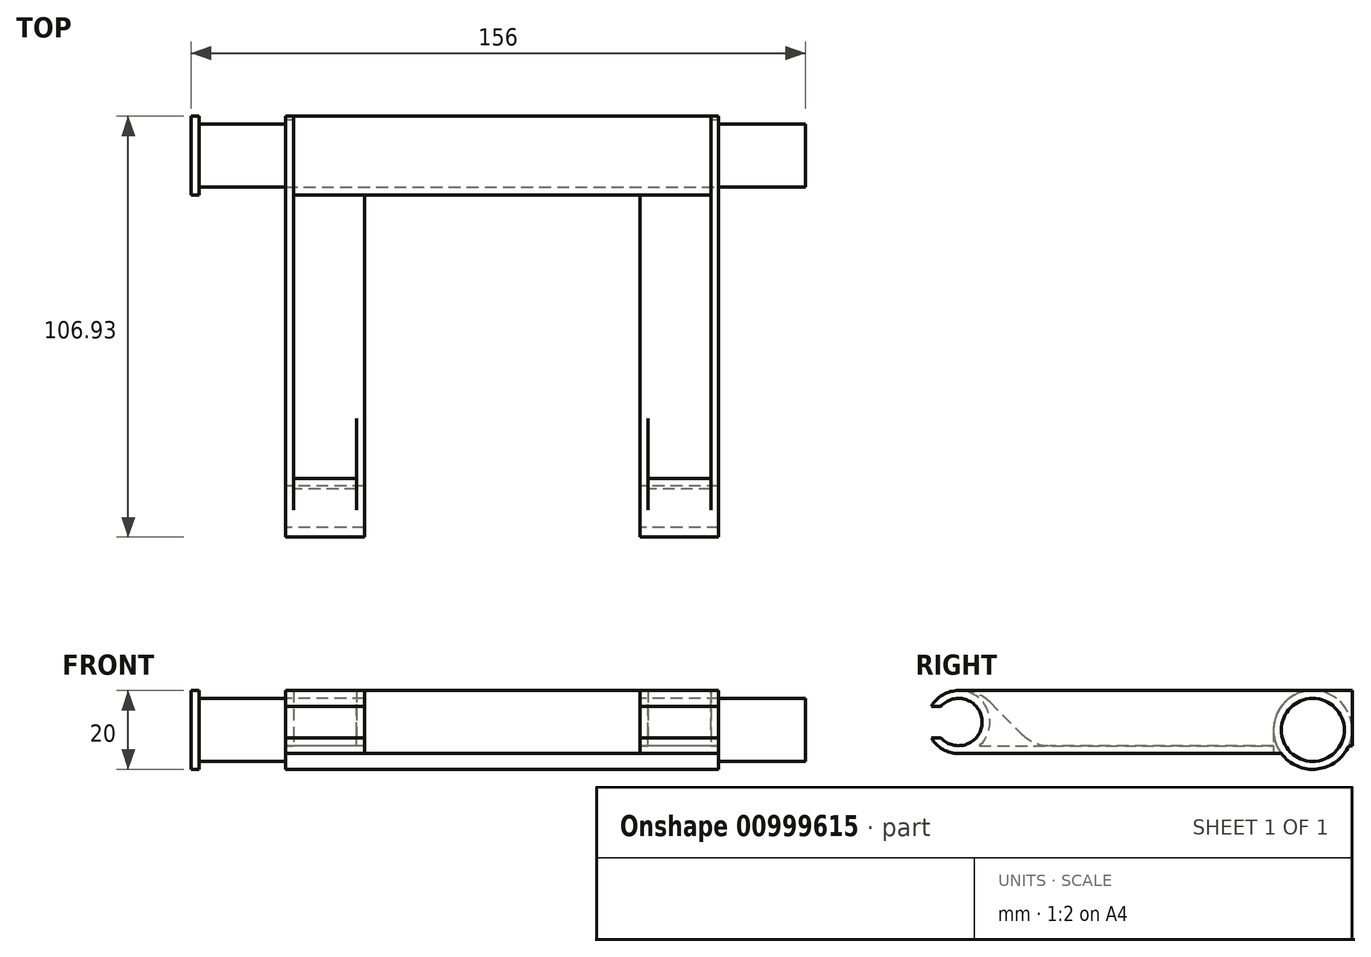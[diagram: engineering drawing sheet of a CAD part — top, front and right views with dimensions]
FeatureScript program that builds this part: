
annotation { "Feature Type Name" : "Feature", "Feature Type Description" : "" }
export const myFeature = defineFeature(function(context is Context, id is Id, definition is map)
    precondition{}
    {
        {
            var Q0;
            Q0=qCreatedBy(makeId("Top.planeOp"),FACE);
            var sketch = newSketch(context, id + "F0", { "sketchPlane" : qUnion([Q0])});
            skLineSegment(sketch, "E0.bottom", {"start": v(55, 40) * mm, "end": v(-55, 40) * mm});
            skLineSegment(sketch, "E0.top", {"start": v(55, -40) * mm, "end": v(-55, -40) * mm});
            skLineSegment(sketch, "E0.left", {"start": v(55, 40) * mm, "end": v(55, -40) * mm});
            skLineSegment(sketch, "E0.right", {"start": v(-55, 40) * mm, "end": v(-55, -40) * mm});
            skPoint(sketch, "E0.middle", {"position": v(0, 0) * mm});
            skLineSegment(sketch, "E1", {"start": v(-55, 40) * mm, "end": v(-55, 60) * mm});
            skLineSegment(sketch, "E2", {"start": v(-55, 60) * mm, "end": v(55, 60) * mm});
            skLineSegment(sketch, "E3", {"start": v(55, 60) * mm, "end": v(55, 40) * mm});
            skSolve(sketch);
        }
        {
            var Q0;
            Q0=makeQuery(id+"F0.imprint","IMPRINT",FACE,{"disambiguationData":[TD([[makeQuery(id+"F0.imprint","IMPRINT",EDGE,{"derivedFrom":sQuery(id+"F0.wireOp",EDGE,"E0.bottom")}),1.0]])]});
            extrude(context, id + "F1", {"entities" : qUnion([Q0]), "depth" : 2 * mm, "offsetDistance" : 25 * mm});
        }
        {
            var Q0;
            Q0=makeQuery(id+"F0.imprint","IMPRINT",FACE,{"disambiguationData":[TD([[makeQuery(id+"F0.imprint","IMPRINT",EDGE,{"derivedFrom":sQuery(id+"F0.wireOp",EDGE,"E0.bottom")}),-1.0]])]});
            extrude(context, id + "F2", {"entities" : qUnion([Q0]), "operationType" : NewBodyOperationType.ADD, "depth" : 16 * mm, "offsetDistance" : 25 * mm});
        }
        {
            var Q0;
            Q0=makeQuery(id+"F0.imprint","IMPRINT",FACE,{"disambiguationData":[TD([[makeQuery(id+"F0.imprint","IMPRINT",EDGE,{"derivedFrom":sQuery(id+"F0.wireOp",EDGE,"E0.bottom")}),-1.0]])]});
            extrude(context, id + "F3", {"entities" : qUnion([Q0]), "operationType" : NewBodyOperationType.ADD, "oppositeDirection" : true, "depth" : 4 * mm, "offsetDistance" : 25 * mm});
        }
        {
            var Q0;
            Q0=qCreatedBy(makeId("Right.planeOp"),FACE);
            var sketch = newSketch(context, id + "F4", { "sketchPlane" : qUnion([Q0])});
            skLineSegment(sketch, "E4.0.0", {"start": v(60, 16) * mm, "end": v(60, -4) * mm});
            skLineSegment(sketch, "E4.0.1", {"start": v(60, -4) * mm, "end": v(40, -4) * mm});
            skLineSegment(sketch, "E4.0.2", {"start": v(40, -4) * mm, "end": v(40, 0) * mm});
            skLineSegment(sketch, "E4.0.3", {"start": v(40, 0) * mm, "end": v(-40, 0) * mm});
            skLineSegment(sketch, "E4.0.4", {"start": v(-40, 0) * mm, "end": v(-40, 2) * mm});
            skLineSegment(sketch, "E4.0.5", {"start": v(-40, 2) * mm, "end": v(40, 2) * mm, "construction": true});
            skLineSegment(sketch, "E4.0.6", {"start": v(40, 2) * mm, "end": v(40, 16) * mm});
            skLineSegment(sketch, "E4.0.7", {"start": v(40, 16) * mm, "end": v(60, 16) * mm});
            skCircle(sketch, "E5", {"center": v(50, 6) * mm, "radius": 10 * mm});
            skPoint(sketch, "E5.centerSnap0", {"position": v(50, 16) * mm});
            skPoint(sketch, "E5.centerSnap1", {"position": v(60, 6) * mm});
            skCircle(sketch, "E6", {"center": v(50, 6) * mm, "radius": 8 * mm});
            skLineSegment(sketch, "E7", {"start": v(40, 0) * mm, "end": v(42, 0) * mm});
            skLineSegment(sketch, "E8", {"start": v(40, 2) * mm, "end": v(40, 0) * mm});
            skLineSegment(sketch, "E9", {"start": v(-40, 2) * mm, "end": v(-40, 8) * mm, "construction": true});
            skCircle(sketch, "E10", {"center": v(-40, 8) * mm, "radius": 8 * mm});
            skCircle(sketch, "E11", {"center": v(-40, 8) * mm, "radius": 6 * mm});
            skLineSegment(sketch, "E12", {"start": v(-40, 4) * mm, "end": v(-50.32, 4) * mm});
            skLineSegment(sketch, "E13", {"start": v(-40, 8) * mm, "end": v(-48, 8) * mm, "construction": true});
            skLineSegment(sketch, "E14.MirrorCS", {"start": v(-40, 12) * mm, "end": v(-50.32, 12) * mm});
            skSolve(sketch);
        }
        {
            var Q0;
            {var subQ0=sQuery(id+"F4.wireOp",EDGE,"E4.0.7");var subQ1=sQuery(id+"F4.wireOp",EDGE,"E4.0.0");var subQ2=makeQuery(id+"F4.imprint","INTERSECT",VERTEX,{"derivedFrom":[subQ1,subQ0]});Q0=makeQuery(id+"F4.imprint","IMPRINT",FACE,{"disambiguationData":[TD([[makeQuery(id+"F4.imprint","IMPRINT",EDGE,{"disambiguationData":[TD([[subQ2,-1.0]])],"derivedFrom":subQ1}),-1.0]])]});}
            var Q1;
            {var subQ0=sQuery(id+"F4.wireOp",EDGE,"E4.0.1");var subQ1=sQuery(id+"F4.wireOp",EDGE,"E4.0.0");var subQ2=makeQuery(id+"F4.imprint","INTERSECT",VERTEX,{"derivedFrom":[subQ1,subQ0]});Q1=makeQuery(id+"F4.imprint","IMPRINT",FACE,{"disambiguationData":[TD([[makeQuery(id+"F4.imprint","IMPRINT",EDGE,{"disambiguationData":[TD([[subQ2,1.0]])],"derivedFrom":subQ1}),-1.0]])]});}
            var Q2;
            {var subQ0=sQuery(id+"F4.wireOp",EDGE,"E4.0.2");Q2=makeQuery(id+"F4.imprint","IMPRINT",FACE,{"disambiguationData":[TD([[makeQuery(id+"F4.imprint","IMPRINT",EDGE,{"derivedFrom":subQ0}),-1.0]])]});}
            var Q3;
            {var subQ0=sQuery(id+"F4.wireOp",EDGE,"E4.0.7");var subQ1=sQuery(id+"F4.wireOp",EDGE,"E4.0.6");var subQ2=makeQuery(id+"F4.imprint","INTERSECT",VERTEX,{"derivedFrom":[subQ1,subQ0]});Q3=makeQuery(id+"F4.imprint","IMPRINT",FACE,{"disambiguationData":[TD([[makeQuery(id+"F4.imprint","IMPRINT",EDGE,{"disambiguationData":[TD([[subQ2,1.0]])],"derivedFrom":subQ1}),-1.0]])]});}
            extrude(context, id + "F5", {"entities" : qUnion([Q0, Q1, Q2, Q3]), "operationType" : NewBodyOperationType.REMOVE, "endBound" : BoundingType.SYMMETRIC, "oppositeDirection" : true, "depth" : 200 * mm, "offsetDistance" : 25 * mm});
        }
        {
            var Q0;
            Q0=makeQuery(id+"F4.imprint","IMPRINT",FACE,{"disambiguationData":[TD([[makeQuery(id+"F4.imprint","IMPRINT",EDGE,{"derivedFrom":sQuery(id+"F4.wireOp",EDGE,"E6")}),1.0]])]});
            extrude(context, id + "F6", {"entities" : qUnion([Q0]), "operationType" : NewBodyOperationType.ADD, "endBound" : BoundingType.SYMMETRIC, "depth" : 154 * mm, "offsetDistance" : 25 * mm});
        }
        {
            var Q0;
            Q0=makeQuery(id+"F6.opExtrude","CAP_FACE",FACE,{"disambiguationData":[OSD([sQuery(id+"F4.wireOp",EDGE,"E6")])],"isStart":true});
            var sketch = newSketch(context, id + "F7", { "sketchPlane" : qUnion([Q0])});
            skCircle(sketch, "E15", {"center": v(-50, 6) * mm, "radius": 10 * mm});
            skSolve(sketch);
        }
        {
            var Q0;
            Q0=makeQuery(id+"F7.imprint","IMPRINT",FACE,{"disambiguationData":[TD([[makeQuery(id+"F7.imprint","IMPRINT",EDGE,{"derivedFrom":sQuery(id+"F7.wireOp",EDGE,"E15")}),1.0]])]});
            var Q1;
            Q1=makeQuery(id+"F7.imprint","IMPRINT",FACE,{"disambiguationData":[TD([[makeQuery(id+"F7.imprint","IMPRINT",EDGE,{"derivedFrom":makeQuery(id+"F6.opExtrude","CAP_EDGE",EDGE,{"disambiguationData":[OSD([sQuery(id+"F4.wireOp",EDGE,"E6")])],"isStart":true})}),-1.0]])]});
            extrude(context, id + "F8", {"entities" : qUnion([Q0, Q1]), "operationType" : NewBodyOperationType.ADD, "depth" : 2 * mm, "offsetDistance" : 25 * mm});
        }
        {
            var Q0;
            Q0=makeQuery(id+"F1.opExtrude","CAP_FACE",FACE,{"disambiguationData":[OSD([sQuery(id+"F0.wireOp",EDGE,"E0.bottom"),sQuery(id+"F0.wireOp",EDGE,"E0.top"),sQuery(id+"F0.wireOp",EDGE,"E0.left"),sQuery(id+"F0.wireOp",EDGE,"E0.right")])],"isStart":false});
            var sketch = newSketch(context, id + "F9", { "sketchPlane" : qUnion([Q0])});
            skLineSegment(sketch, "E16", {"start": v(-55, 60) * mm, "end": v(55, 60) * mm});
            skLineSegment(sketch, "E17", {"start": v(-55, 60) * mm, "end": v(-55, -40) * mm});
            skLineSegment(sketch, "E18", {"start": v(-55, -40) * mm, "end": v(-53, -40) * mm});
            skLineSegment(sketch, "E19", {"start": v(-53, -40) * mm, "end": v(-53, 60) * mm});
            skLineSegment(sketch, "E20", {"start": v(55, 60) * mm, "end": v(55, -40) * mm});
            skLineSegment(sketch, "E21", {"start": v(55, -40) * mm, "end": v(53, -40) * mm});
            skLineSegment(sketch, "E22", {"start": v(53, -40) * mm, "end": v(53, 60) * mm});
            skLineSegment(sketch, "E23", {"start": v(-55, 50) * mm, "end": v(55, 50) * mm});
            skLineSegment(sketch, "E24", {"start": v(-35, -40) * mm, "end": v(-35, 40) * mm});
            skLineSegment(sketch, "E25", {"start": v(-35, -40) * mm, "end": v(-37, -40) * mm});
            skLineSegment(sketch, "E26", {"start": v(-37, -40) * mm, "end": v(-37, 40) * mm});
            skLineSegment(sketch, "E27", {"start": v(-37, 40) * mm, "end": v(-35, 40) * mm});
            skLineSegment(sketch, "E28", {"start": v(-37, 40) * mm, "end": v(-37, 50) * mm});
            skLineSegment(sketch, "E29", {"start": v(-35, 40) * mm, "end": v(-35, 50) * mm});
            skLineSegment(sketch, "E30", {"start": v(0, 0) * mm, "end": v(0, 23.43) * mm, "construction": true});
            skLineSegment(sketch, "E31.MirrorCS", {"start": v(37, -40) * mm, "end": v(37, 40) * mm});
            skLineSegment(sketch, "E32.MirrorCS", {"start": v(35, -40) * mm, "end": v(35, 40) * mm});
            skLineSegment(sketch, "E33.MirrorCS", {"start": v(35, -40) * mm, "end": v(37, -40) * mm});
            skLineSegment(sketch, "E34.MirrorCS", {"start": v(37, 40) * mm, "end": v(35, 40) * mm});
            skLineSegment(sketch, "E35.MirrorCS", {"start": v(37, 40) * mm, "end": v(37, 50) * mm});
            skLineSegment(sketch, "E36.MirrorCS", {"start": v(35, 40) * mm, "end": v(35, 50) * mm});
            skLineSegment(sketch, "E37", {"start": v(-37, -15) * mm, "end": v(-35, -15) * mm});
            skLineSegment(sketch, "E38.MirrorCS", {"start": v(37, -15) * mm, "end": v(35, -15) * mm});
            skSolve(sketch);
        }
        {
            var Q0;
            {var subQ0=sQuery(id+"F9.wireOp",EDGE,"E18");Q0=makeQuery(id+"F9.imprint","IMPRINT",FACE,{"disambiguationData":[TD([[makeQuery(id+"F9.imprint","IMPRINT",EDGE,{"derivedFrom":subQ0}),-1.0]])]});}
            var Q1;
            {var subQ0=sQuery(id+"F9.wireOp",EDGE,"E17");var subQ1=makeQuery(id+"F1.opExtrude","CAP_EDGE",EDGE,{"disambiguationData":[OSD([sQuery(id+"F0.wireOp",EDGE,"E0.bottom")])],"isStart":false});var subQ2=makeQuery(id+"F9.imprint","INTERSECT",VERTEX,{"derivedFrom":[subQ1,subQ0]});Q1=makeQuery(id+"F9.imprint","IMPRINT",FACE,{"disambiguationData":[TD([[makeQuery(id+"F9.imprint","IMPRINT",EDGE,{"disambiguationData":[TD([[subQ2,1.0]])],"derivedFrom":subQ0}),1.0]])]});}
            var Q2;
            {var subQ0=sQuery(id+"F9.wireOp",EDGE,"E21");Q2=makeQuery(id+"F9.imprint","IMPRINT",FACE,{"disambiguationData":[TD([[makeQuery(id+"F9.imprint","IMPRINT",EDGE,{"derivedFrom":subQ0}),-1.0]])]});}
            var Q3;
            {var subQ0=sQuery(id+"F9.wireOp",EDGE,"E20");var subQ1=makeQuery(id+"F1.opExtrude","CAP_EDGE",EDGE,{"disambiguationData":[OSD([sQuery(id+"F0.wireOp",EDGE,"E0.bottom")])],"isStart":false});var subQ2=makeQuery(id+"F9.imprint","INTERSECT",VERTEX,{"derivedFrom":[subQ1,subQ0]});Q3=makeQuery(id+"F9.imprint","IMPRINT",FACE,{"disambiguationData":[TD([[makeQuery(id+"F9.imprint","IMPRINT",EDGE,{"disambiguationData":[TD([[subQ2,1.0]])],"derivedFrom":subQ0}),-1.0]])]});}
            var Q4;
            {var subQ0=sQuery(id+"F9.wireOp",EDGE,"E25");Q4=makeQuery(id+"F9.imprint","IMPRINT",FACE,{"disambiguationData":[TD([[makeQuery(id+"F9.imprint","IMPRINT",EDGE,{"derivedFrom":subQ0}),-1.0]])]});}
            var Q5;
            {var subQ0=sQuery(id+"F9.wireOp",EDGE,"E33.MirrorCS");Q5=makeQuery(id+"F9.imprint","IMPRINT",FACE,{"disambiguationData":[TD([[makeQuery(id+"F9.imprint","IMPRINT",EDGE,{"derivedFrom":subQ0}),-1.0]])]});}
            extrude(context, id + "F10", {"entities" : qUnion([Q0, Q1, Q2, Q3, Q4, Q5]), "operationType" : NewBodyOperationType.ADD, "depth" : 14 * mm, "offsetDistance" : 25 * mm});
        }
        {
            var Q0;
            {var subQ1=sQuery(id+"F4.wireOp",EDGE,"E4.0.4");var subQ3=sQuery(id+"F4.wireOp",EDGE,"E11");var subQ4=makeQuery(id+"F4.imprint","INTERSECT",VERTEX,{"derivedFrom":[subQ1,subQ3]});Q0=makeQuery(id+"F4.imprint","IMPRINT",FACE,{"disambiguationData":[TD([[makeQuery(id+"F4.imprint","IMPRINT",EDGE,{"disambiguationData":[TD([[subQ4,1.0]])],"derivedFrom":subQ3}),-1.0]])]});}
            var Q1;
            {var subQ0=sQuery(id+"F4.wireOp",EDGE,"E4.0.4");Q1=makeQuery(id+"F4.imprint","IMPRINT",FACE,{"disambiguationData":[TD([[makeQuery(id+"F4.imprint","IMPRINT",EDGE,{"derivedFrom":subQ0}),-1.0]])]});}
            extrude(context, id + "F11", {"entities" : qUnion([Q0, Q1]), "operationType" : NewBodyOperationType.ADD, "endBound" : BoundingType.SYMMETRIC, "depth" : 110 * mm, "offsetDistance" : 25 * mm});
        }
        {
            var Q0;
            {var subQ3=sQuery(id+"F4.wireOp",EDGE,"E11");var subQ5=makeQuery(id+"F4.imprint","INTERSECT",VERTEX,{"derivedFrom":[subQ3,sQuery(id+"F4.wireOp",EDGE,"E14.MirrorCS")]});Q0=makeQuery(id+"F4.imprint","IMPRINT",FACE,{"disambiguationData":[TD([[makeQuery(id+"F4.imprint","IMPRINT",EDGE,{"disambiguationData":[TD([[subQ5,-1.0]])],"derivedFrom":subQ3}),1.0]])]});}
            var Q1;
            {var subQ1=sQuery(id+"F4.wireOp",EDGE,"E4.0.4");var subQ3=sQuery(id+"F4.wireOp",EDGE,"E11");var subQ4=makeQuery(id+"F4.imprint","INTERSECT",VERTEX,{"derivedFrom":[subQ1,subQ3]});Q1=makeQuery(id+"F4.imprint","IMPRINT",FACE,{"disambiguationData":[TD([[makeQuery(id+"F4.imprint","IMPRINT",EDGE,{"disambiguationData":[TD([[subQ4,-1.0]])],"derivedFrom":subQ3}),1.0]])]});}
            var Q2;
            {var subQ1=sQuery(id+"F4.wireOp",EDGE,"E4.0.4");var subQ3=sQuery(id+"F4.wireOp",EDGE,"E11");var subQ4=makeQuery(id+"F4.imprint","INTERSECT",VERTEX,{"derivedFrom":[subQ1,subQ3]});Q2=makeQuery(id+"F4.imprint","IMPRINT",FACE,{"disambiguationData":[TD([[makeQuery(id+"F4.imprint","IMPRINT",EDGE,{"disambiguationData":[TD([[subQ4,1.0]])],"derivedFrom":subQ3}),1.0]])]});}
            extrude(context, id + "F12", {"entities" : qUnion([Q0, Q1, Q2]), "operationType" : NewBodyOperationType.REMOVE, "endBound" : BoundingType.SYMMETRIC, "oppositeDirection" : true, "depth" : 200 * mm, "offsetDistance" : 25 * mm});
        }
        {
            var Q0;
            {var subQ0=sQuery(id+"F0.wireOp",EDGE,"E0.bottom");Q0=makeQuery(id+"F5.boolean.opBoolean","MERGE",FACE,{"derivedFrom":[makeQuery(id+"F2.boolean.opBoolean","MERGE",FACE,{"derivedFrom":[makeQuery(id+"F1.opExtrude","CAP_FACE",FACE,{"disambiguationData":[OSD([subQ0,sQuery(id+"F0.wireOp",EDGE,"E0.top"),sQuery(id+"F0.wireOp",EDGE,"E0.left"),sQuery(id+"F0.wireOp",EDGE,"E0.right")])],"isStart":true}),makeQuery(id+"F2.opExtrude","CAP_FACE",FACE,{"disambiguationData":[OSD([subQ0,sQuery(id+"F0.wireOp",EDGE,"E1"),sQuery(id+"F0.wireOp",EDGE,"E2"),sQuery(id+"F0.wireOp",EDGE,"E3")])],"isStart":true})]})],"fromTools":[makeQuery(id+"F5.opExtrude","SWEPT_FACE",FACE,{"disambiguationData":[OSD([sQuery(id+"F4.wireOp",EDGE,"E7")])]})]});}
            var sketch = newSketch(context, id + "F13", { "sketchPlane" : qUnion([Q0])});
            skLineSegment(sketch, "E39.0", {"start": v(-55, -42) * mm, "end": v(55, -42) * mm});
            skLineSegment(sketch, "E40.0", {"start": v(55, -42) * mm, "end": v(55, 40) * mm});
            skLineSegment(sketch, "E41.0", {"start": v(-55, -42) * mm, "end": v(-55, 40) * mm});
            skLineSegment(sketch, "E42.0", {"start": v(55, 40) * mm, "end": v(-55, 40) * mm});
            skLineSegment(sketch, "E43.0", {"start": v(55, 46.93) * mm, "end": v(-55, 46.93) * mm});
            skLineSegment(sketch, "E44", {"start": v(-35, 46.93) * mm, "end": v(-35, -42) * mm});
            skLineSegment(sketch, "E45", {"start": v(35, 46.93) * mm, "end": v(35, -42) * mm});
            skLineSegment(sketch, "E46", {"start": v(55, -60) * mm, "end": v(-55, -60) * mm});
            skLineSegment(sketch, "E47.0", {"start": v(-53, -40) * mm, "end": v(53, -40) * mm});
            skSolve(sketch);
        }
        {
            var Q0;
            {var subQ0=sQuery(id+"F13.wireOp",EDGE,"E45");var subQ1=sQuery(id+"F13.wireOp",EDGE,"E42.0");var subQ2=makeQuery(id+"F13.imprint","INTERSECT",VERTEX,{"derivedFrom":[subQ1,subQ0]});Q0=makeQuery(id+"F13.imprint","IMPRINT",FACE,{"disambiguationData":[TD([[makeQuery(id+"F13.imprint","IMPRINT",EDGE,{"disambiguationData":[TD([[subQ2,-1.0]])],"derivedFrom":subQ1}),1.0]])]});}
            var Q1;
            {var subQ0=sQuery(id+"F13.wireOp",EDGE,"E45");var subQ1=sQuery(id+"F13.wireOp",EDGE,"E42.0");var subQ2=makeQuery(id+"F13.imprint","INTERSECT",VERTEX,{"derivedFrom":[subQ1,subQ0]});Q1=makeQuery(id+"F13.imprint","IMPRINT",FACE,{"disambiguationData":[TD([[makeQuery(id+"F13.imprint","IMPRINT",EDGE,{"disambiguationData":[TD([[subQ2,-1.0]])],"derivedFrom":subQ1}),-1.0]])]});}
            extrude(context, id + "F14", {"entities" : qUnion([Q0, Q1]), "operationType" : NewBodyOperationType.REMOVE, "oppositeDirection" : true, "depth" : 25 * mm, "offsetDistance" : 25 * mm});
        }
        {
            var Q0;
            Q0=makeQuery(id+"F10.opExtrude","CAP_EDGE",EDGE,{"disambiguationData":[OSD([sQuery(id+"F9.wireOp",EDGE,"E38.MirrorCS")])],"isStart":false});
            var Q1;
            Q1=makeQuery(id+"F10.opExtrude","CAP_EDGE",EDGE,{"disambiguationData":[OSD([sQuery(id+"F9.wireOp",EDGE,"E37")])],"isStart":false});
            chamfer(context, id + "F15", {"entities" : qUnion([Q0, Q1]), "width" : 20 * mm, "tangentPropagation" : true});
        }
        {
            var Q0;
            {var subQ0=sQuery(id+"F9.wireOp",EDGE,"E37");Q0=makeQuery(id+"F15.opChamfer","BLEND_EDGE",EDGE,{"blendedFrom":[makeQuery(id+"F10.opExtrude","CAP_EDGE",EDGE,{"disambiguationData":[OSD([subQ0])],"isStart":false}),makeQuery(id+"F10.opExtrude","CAP_FACE",FACE,{"disambiguationData":[OSD([sQuery(id+"F9.wireOp",EDGE,"E24"),sQuery(id+"F9.wireOp",EDGE,"E25"),sQuery(id+"F9.wireOp",EDGE,"E26"),subQ0])],"isStart":false})],"blendedInto":[makeQuery(id+"F10.opExtrude","CAP_FACE",FACE,{"disambiguationData":[OSD([sQuery(id+"F9.wireOp",EDGE,"E24"),sQuery(id+"F9.wireOp",EDGE,"E25"),sQuery(id+"F9.wireOp",EDGE,"E26"),subQ0])],"isStart":false})]});}
            var Q1;
            {var subQ0=sQuery(id+"F9.wireOp",EDGE,"E38.MirrorCS");Q1=makeQuery(id+"F15.opChamfer","BLEND_EDGE",EDGE,{"blendedFrom":[makeQuery(id+"F10.opExtrude","CAP_EDGE",EDGE,{"disambiguationData":[OSD([subQ0])],"isStart":false}),makeQuery(id+"F10.opExtrude","CAP_FACE",FACE,{"disambiguationData":[OSD([sQuery(id+"F9.wireOp",EDGE,"E31.MirrorCS"),sQuery(id+"F9.wireOp",EDGE,"E32.MirrorCS"),sQuery(id+"F9.wireOp",EDGE,"E33.MirrorCS"),subQ0])],"isStart":false})],"blendedInto":[makeQuery(id+"F10.opExtrude","CAP_FACE",FACE,{"disambiguationData":[OSD([sQuery(id+"F9.wireOp",EDGE,"E31.MirrorCS"),sQuery(id+"F9.wireOp",EDGE,"E32.MirrorCS"),sQuery(id+"F9.wireOp",EDGE,"E33.MirrorCS"),subQ0])],"isStart":false})]});}
            var Q2;
            {var subQ0=makeQuery(id+"F10.opExtrude","SWEPT_FACE",FACE,{"disambiguationData":[OSD([sQuery(id+"F9.wireOp",EDGE,"E32.MirrorCS")])]});var subQ1=makeQuery(id+"F10.opExtrude","SWEPT_FACE",FACE,{"disambiguationData":[OSD([sQuery(id+"F9.wireOp",EDGE,"E22")])]});var subQ2=makeQuery(id+"F10.opExtrude","SWEPT_FACE",FACE,{"disambiguationData":[OSD([sQuery(id+"F9.wireOp",EDGE,"E31.MirrorCS")])]});var subQ3=sQuery(id+"F0.wireOp",EDGE,"E0.bottom");var subQ4=makeQuery(id+"F2.opExtrude","SWEPT_FACE",FACE,{"disambiguationData":[OSD([subQ3])]});var subQ5=sQuery(id+"F9.wireOp",EDGE,"E38.MirrorCS");var subQ6=makeQuery(id+"F10.opExtrude","SWEPT_FACE",FACE,{"disambiguationData":[OSD([subQ5])]});var subQ7=makeQuery(id+"F11.opExtrude","SWEPT_FACE",FACE,{"disambiguationData":[OSD([sQuery(id+"F4.wireOp",EDGE,"E10")])]});Q2=makeQuery(id+"F15.opChamfer","BLEND_EDGE",EDGE,{"blendedFrom":[makeQuery(id+"F10.opExtrude","CAP_EDGE",EDGE,{"disambiguationData":[OSD([subQ5])],"isStart":false}),makeQuery(id+"F14.boolean.opBoolean","SPLIT",FACE,{"disambiguationData":[TD([subQ1])],"derivedFrom":makeQuery(id+"F11.boolean.opBoolean","SPLIT",FACE,{"disambiguationData":[TD([subQ4,makeQuery(id+"F10.opExtrude","SWEPT_FACE",FACE,{"disambiguationData":[OSD([sQuery(id+"F9.wireOp",EDGE,"E19")])]}),subQ1,makeQuery(id+"F10.opExtrude","SWEPT_FACE",FACE,{"disambiguationData":[OSD([sQuery(id+"F9.wireOp",EDGE,"E24")])]}),makeQuery(id+"F10.opExtrude","SWEPT_FACE",FACE,{"disambiguationData":[OSD([sQuery(id+"F9.wireOp",EDGE,"E26")])]}),subQ2,subQ0,makeQuery(id+"F10.opExtrude","SWEPT_FACE",FACE,{"disambiguationData":[OSD([sQuery(id+"F9.wireOp",EDGE,"E37")])]}),subQ6,subQ7])],"derivedFrom":makeQuery(id+"F1.opExtrude","CAP_FACE",FACE,{"disambiguationData":[OSD([subQ3,sQuery(id+"F0.wireOp",EDGE,"E0.top"),sQuery(id+"F0.wireOp",EDGE,"E0.left"),sQuery(id+"F0.wireOp",EDGE,"E0.right")])],"isStart":false})})})],"blendedInto":[makeQuery(id+"F14.boolean.opBoolean","SPLIT",FACE,{"disambiguationData":[TD([subQ1])],"derivedFrom":makeQuery(id+"F11.boolean.opBoolean","SPLIT",FACE,{"disambiguationData":[TD([subQ4,makeQuery(id+"F10.opExtrude","SWEPT_FACE",FACE,{"disambiguationData":[OSD([sQuery(id+"F9.wireOp",EDGE,"E19")])]}),subQ1,makeQuery(id+"F10.opExtrude","SWEPT_FACE",FACE,{"disambiguationData":[OSD([sQuery(id+"F9.wireOp",EDGE,"E24")])]}),makeQuery(id+"F10.opExtrude","SWEPT_FACE",FACE,{"disambiguationData":[OSD([sQuery(id+"F9.wireOp",EDGE,"E26")])]}),subQ2,subQ0,makeQuery(id+"F10.opExtrude","SWEPT_FACE",FACE,{"disambiguationData":[OSD([sQuery(id+"F9.wireOp",EDGE,"E37")])]}),subQ6,subQ7])],"derivedFrom":makeQuery(id+"F1.opExtrude","CAP_FACE",FACE,{"disambiguationData":[OSD([subQ3,sQuery(id+"F0.wireOp",EDGE,"E0.top"),sQuery(id+"F0.wireOp",EDGE,"E0.left"),sQuery(id+"F0.wireOp",EDGE,"E0.right")])],"isStart":false})})})]});}
            var Q3;
            {var subQ0=makeQuery(id+"F10.opExtrude","SWEPT_FACE",FACE,{"disambiguationData":[OSD([sQuery(id+"F9.wireOp",EDGE,"E26")])]});var subQ1=sQuery(id+"F0.wireOp",EDGE,"E0.bottom");var subQ2=makeQuery(id+"F2.opExtrude","SWEPT_FACE",FACE,{"disambiguationData":[OSD([subQ1])]});var subQ3=makeQuery(id+"F10.opExtrude","SWEPT_FACE",FACE,{"disambiguationData":[OSD([sQuery(id+"F9.wireOp",EDGE,"E19")])]});var subQ4=makeQuery(id+"F10.opExtrude","SWEPT_FACE",FACE,{"disambiguationData":[OSD([sQuery(id+"F9.wireOp",EDGE,"E24")])]});var subQ5=sQuery(id+"F9.wireOp",EDGE,"E37");var subQ6=makeQuery(id+"F10.opExtrude","SWEPT_FACE",FACE,{"disambiguationData":[OSD([subQ5])]});var subQ7=makeQuery(id+"F11.opExtrude","SWEPT_FACE",FACE,{"disambiguationData":[OSD([sQuery(id+"F4.wireOp",EDGE,"E10")])]});Q3=makeQuery(id+"F15.opChamfer","BLEND_EDGE",EDGE,{"blendedFrom":[makeQuery(id+"F10.opExtrude","CAP_EDGE",EDGE,{"disambiguationData":[OSD([subQ5])],"isStart":false}),makeQuery(id+"F14.boolean.opBoolean","SPLIT",FACE,{"disambiguationData":[TD([subQ3])],"derivedFrom":makeQuery(id+"F11.boolean.opBoolean","SPLIT",FACE,{"disambiguationData":[TD([subQ2,subQ3,makeQuery(id+"F10.opExtrude","SWEPT_FACE",FACE,{"disambiguationData":[OSD([sQuery(id+"F9.wireOp",EDGE,"E22")])]}),subQ4,subQ0,makeQuery(id+"F10.opExtrude","SWEPT_FACE",FACE,{"disambiguationData":[OSD([sQuery(id+"F9.wireOp",EDGE,"E31.MirrorCS")])]}),makeQuery(id+"F10.opExtrude","SWEPT_FACE",FACE,{"disambiguationData":[OSD([sQuery(id+"F9.wireOp",EDGE,"E32.MirrorCS")])]}),subQ6,makeQuery(id+"F10.opExtrude","SWEPT_FACE",FACE,{"disambiguationData":[OSD([sQuery(id+"F9.wireOp",EDGE,"E38.MirrorCS")])]}),subQ7])],"derivedFrom":makeQuery(id+"F1.opExtrude","CAP_FACE",FACE,{"disambiguationData":[OSD([subQ1,sQuery(id+"F0.wireOp",EDGE,"E0.top"),sQuery(id+"F0.wireOp",EDGE,"E0.left"),sQuery(id+"F0.wireOp",EDGE,"E0.right")])],"isStart":false})})})],"blendedInto":[makeQuery(id+"F14.boolean.opBoolean","SPLIT",FACE,{"disambiguationData":[TD([subQ3])],"derivedFrom":makeQuery(id+"F11.boolean.opBoolean","SPLIT",FACE,{"disambiguationData":[TD([subQ2,subQ3,makeQuery(id+"F10.opExtrude","SWEPT_FACE",FACE,{"disambiguationData":[OSD([sQuery(id+"F9.wireOp",EDGE,"E22")])]}),subQ4,subQ0,makeQuery(id+"F10.opExtrude","SWEPT_FACE",FACE,{"disambiguationData":[OSD([sQuery(id+"F9.wireOp",EDGE,"E31.MirrorCS")])]}),makeQuery(id+"F10.opExtrude","SWEPT_FACE",FACE,{"disambiguationData":[OSD([sQuery(id+"F9.wireOp",EDGE,"E32.MirrorCS")])]}),subQ6,makeQuery(id+"F10.opExtrude","SWEPT_FACE",FACE,{"disambiguationData":[OSD([sQuery(id+"F9.wireOp",EDGE,"E38.MirrorCS")])]}),subQ7])],"derivedFrom":makeQuery(id+"F1.opExtrude","CAP_FACE",FACE,{"disambiguationData":[OSD([subQ1,sQuery(id+"F0.wireOp",EDGE,"E0.top"),sQuery(id+"F0.wireOp",EDGE,"E0.left"),sQuery(id+"F0.wireOp",EDGE,"E0.right")])],"isStart":false})})})]});}
            fillet(context, id + "F16", {"entities" : qUnion([Q0, Q1, Q2, Q3]), "radius" : 10 * mm, "tangentPropagation" : true, "allowEdgeOverflow" : false});
        }
        {
            var Q0;
            {var subQ1=sQuery(id+"F4.wireOp",EDGE,"E12");Q0=makeQuery(id+"F14.boolean.opBoolean","SPLIT",FACE,{"disambiguationData":[TD([makeQuery(id+"F1.opExtrude","SWEPT_FACE",FACE,{"disambiguationData":[OSD([sQuery(id+"F0.wireOp",EDGE,"E0.left")])]})])],"derivedFrom":makeQuery(id+"F11.opExtrude","SWEPT_FACE",FACE,{"disambiguationData":[OSD([subQ1])]})});}
            cPlane(context, id + "F17", {"entities" : qUnion([Q0]), "cplaneType" : CPlaneType.OFFSET, "offset" : 4 * mm, "width" : 150 * mm, "height" : 150 * mm});
        }
    });
